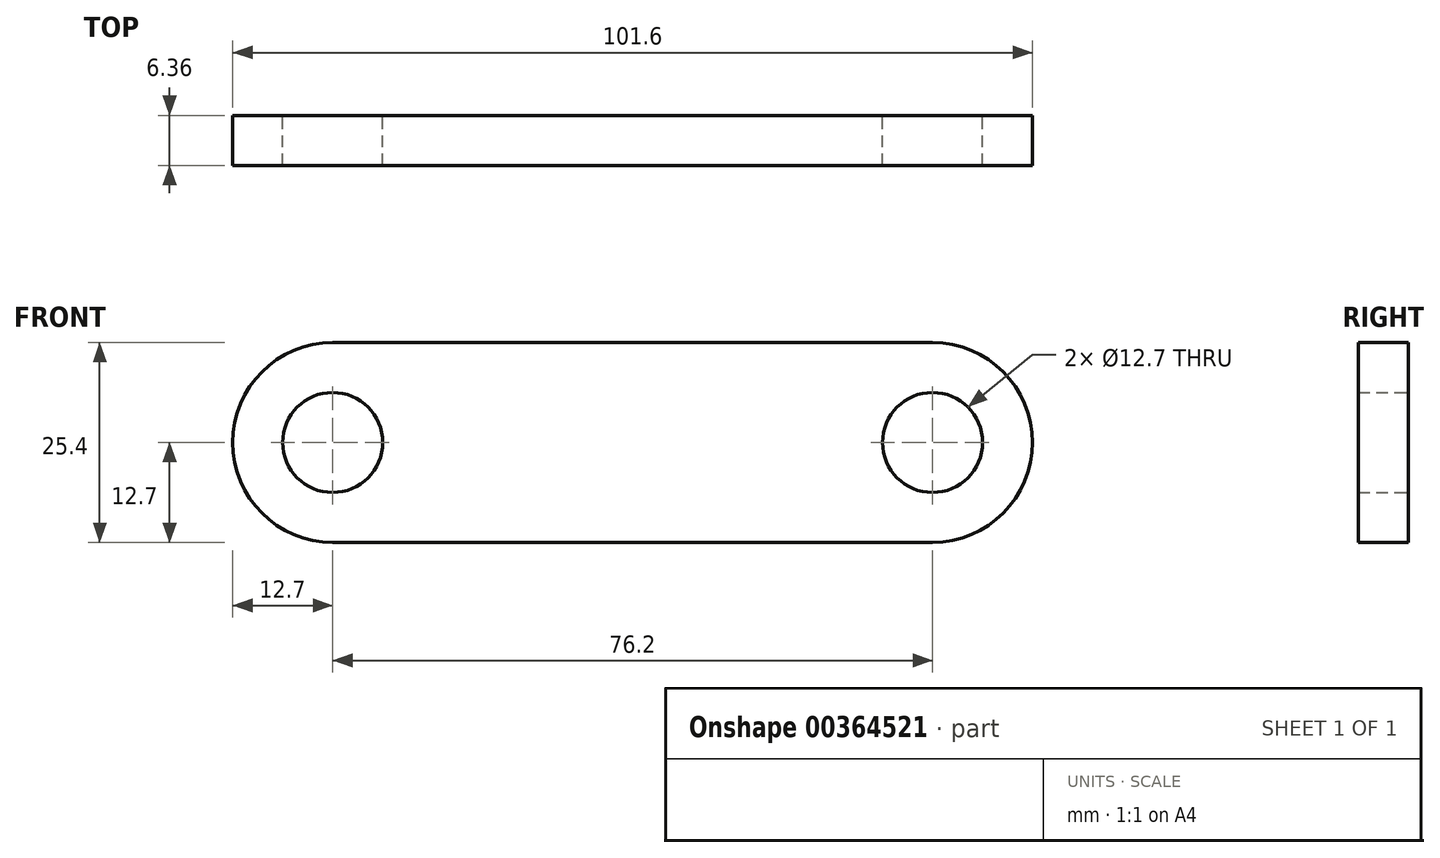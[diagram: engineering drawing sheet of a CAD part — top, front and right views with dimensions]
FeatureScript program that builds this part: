
annotation { "Feature Type Name" : "Feature", "Feature Type Description" : "" }
export const myFeature = defineFeature(function(context is Context, id is Id, definition is map)
    precondition{}
    {
        {
            var Q0;
            Q0=qCreatedBy(makeId("Front.planeOp"),FACE);
            var sketch = newSketch(context, id + "F0", { "sketchPlane" : qUnion([Q0])});
            skLineSegment(sketch, "E0", {"start": v(-38.1, 0) * mm, "end": v(38.1, 0) * mm, "construction": true});
            skArc(sketch, "E1.0.startCap", {"start": v(-38.1, -12.7) * mm, "mid": v(-50.8, 0) * mm, "end": v(-38.1, 12.7) * mm});
            skArc(sketch, "E1.0.endCap", {"start": v(38.1, 12.7) * mm, "mid": v(50.8, 0) * mm, "end": v(38.1, -12.7) * mm});
            skLineSegment(sketch, "E1.0.left", {"start": v(-38.1, 12.7) * mm, "end": v(38.1, 12.7) * mm});
            skLineSegment(sketch, "E1.0.right", {"start": v(-38.1, -12.7) * mm, "end": v(38.1, -12.7) * mm});
            skCircle(sketch, "E2", {"center": v(-38.1, 0) * mm, "radius": 6.35 * mm});
            skCircle(sketch, "E3", {"center": v(38.1, 0) * mm, "radius": 6.35 * mm});
            skSolve(sketch);
        }
        {
            var Q0;
            Q0 = qSketchRegion(id + "F0", true);
            extrude(context, id + "F1", {"entities" : qUnion([Q0]), "endBound" : BoundingType.SYMMETRIC, "depth" : 6.35 * mm});
        }
    });
